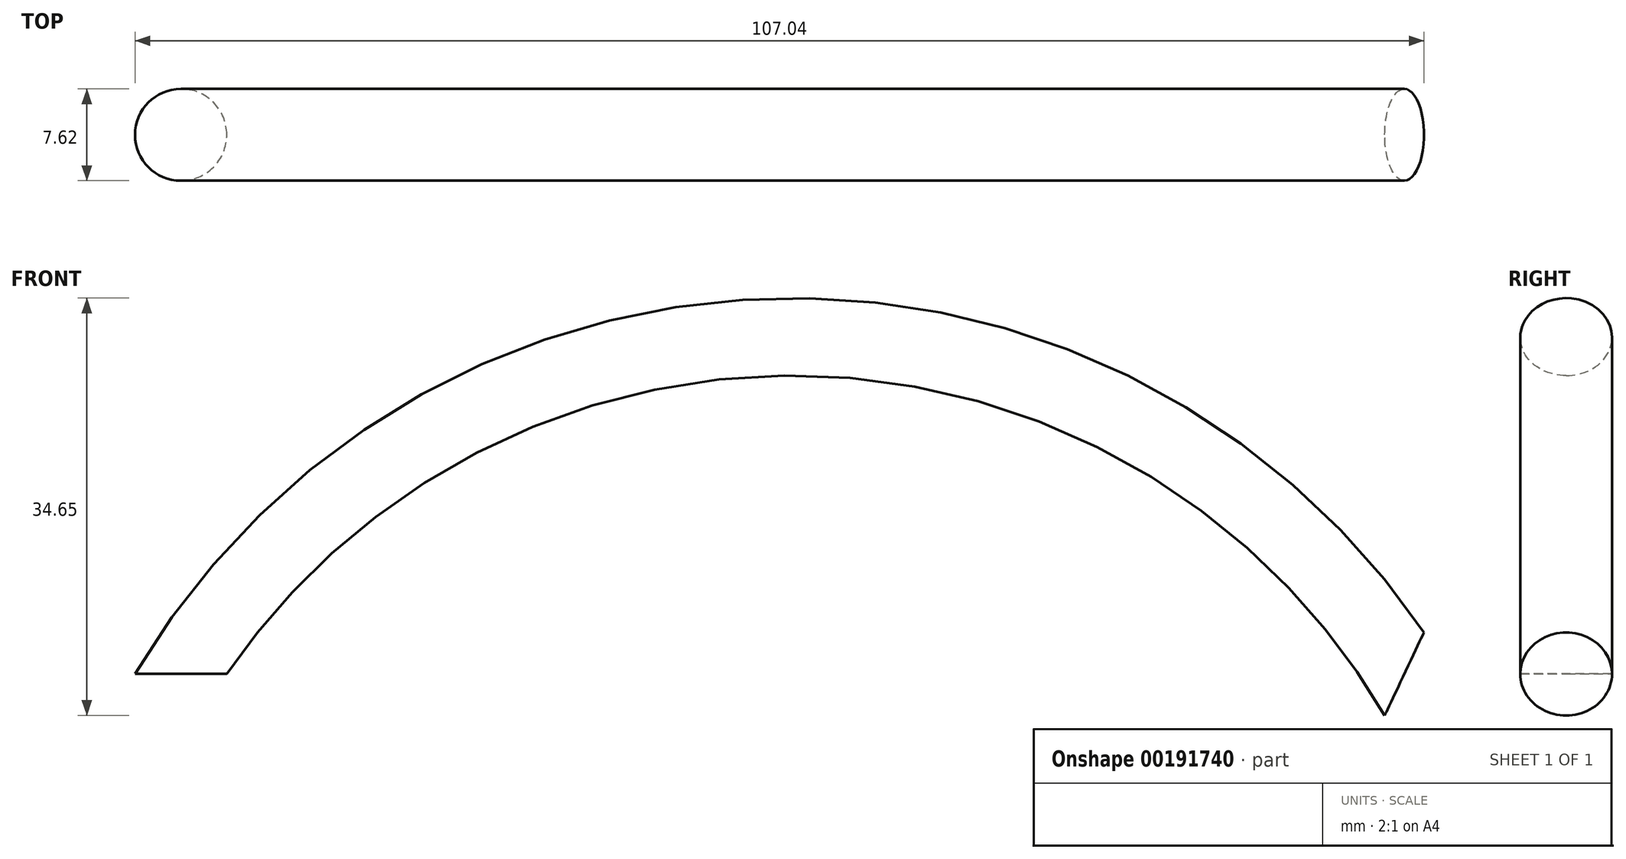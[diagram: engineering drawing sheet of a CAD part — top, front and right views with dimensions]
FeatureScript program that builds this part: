
annotation { "Feature Type Name" : "Feature", "Feature Type Description" : "" }
export const myFeature = defineFeature(function(context is Context, id is Id, definition is map)
    precondition{}
    {
        {
            var Q0;
            Q0=qCreatedBy(makeId("Front.planeOp"),FACE);
            var sketch = newSketch(context, id + "F0", { "sketchPlane" : qUnion([Q0])});
            skArc(sketch, "E0", {"start": v(52.27, 0) * mm, "mid": v(1.47, 27.96) * mm, "end": v(-49.33, 0) * mm});
            skSolve(sketch);
        }
        {
            var Q0;
            Q0=qCreatedBy(makeId("Top.planeOp"),FACE);
            var sketch = newSketch(context, id + "F1", { "sketchPlane" : qUnion([Q0])});
            skCircle(sketch, "E1", {"center": v(-49.33, 0) * mm, "radius": 3.8 * mm});
            skSolve(sketch);
        }
        {
            var Q0;
            Q0=makeQuery(id+"F1.imprint","IMPRINT",FACE,{"disambiguationData":[TD([[makeQuery(id+"F1.imprint","IMPRINT",EDGE,{"derivedFrom":sQuery(id+"F1.wireOp",EDGE,"E1")}),1.0]])]});
            var Q1;
            Q1 = qConstructionFilter(qBodyType(qCreatedBy(id + "F0" ,EDGE), BodyType.WIRE), ConstructionObject.NO);
            sweep(context, id + "F2", {"profiles" : qUnion([Q0]), "path" : qUnion([Q1])});
        }
    });
